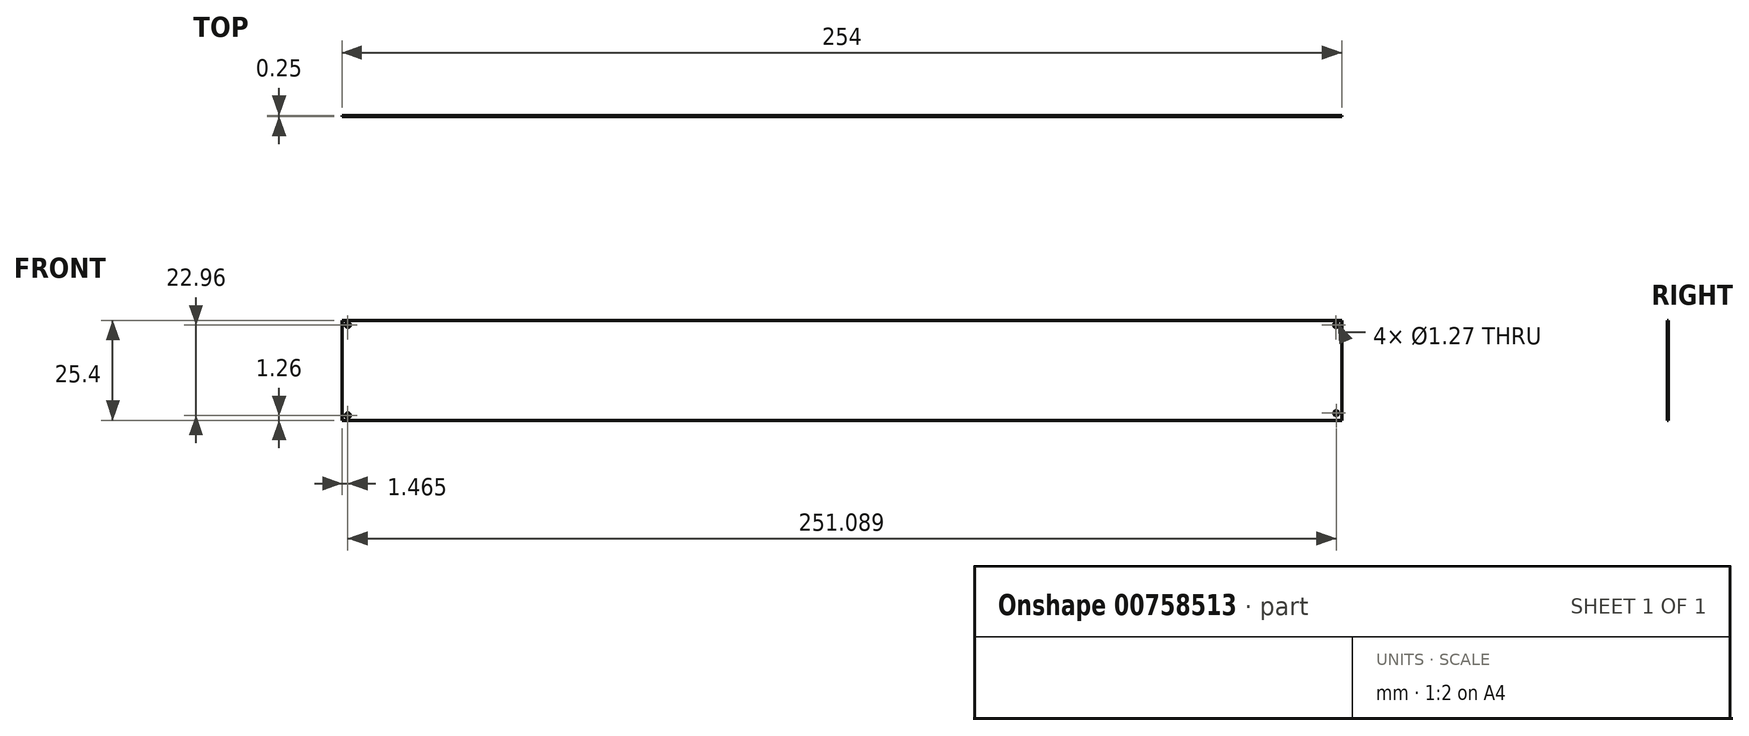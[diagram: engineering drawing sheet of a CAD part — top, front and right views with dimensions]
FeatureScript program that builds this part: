
annotation { "Feature Type Name" : "Feature", "Feature Type Description" : "" }
export const myFeature = defineFeature(function(context is Context, id is Id, definition is map)
    precondition{}
    {
        {
            var Q0;
            Q0=qCreatedBy(makeId("Front.planeOp"),FACE);
            var sketch = newSketch(context, id + "F0", { "sketchPlane" : qUnion([Q0])});
            skLineSegment(sketch, "E0.bottom", {"start": v(-49.32, 25.4) * mm, "end": v(204.68, 25.4) * mm});
            skLineSegment(sketch, "E0.top", {"start": v(-49.32, 0) * mm, "end": v(204.68, 0) * mm});
            skLineSegment(sketch, "E0.left", {"start": v(-49.32, 25.4) * mm, "end": v(-49.32, 0) * mm});
            skLineSegment(sketch, "E0.right", {"start": v(204.68, 25.4) * mm, "end": v(204.68, 0) * mm});
            skSolve(sketch);
        }
        {
            var Q0;
            Q0=makeQuery(id+"F0.imprint","IMPRINT",FACE,{"disambiguationData":[TD([[makeQuery(id+"F0.imprint","IMPRINT",EDGE,{"derivedFrom":sQuery(id+"F0.wireOp",EDGE,"E0.bottom")}),-1.0]])]});
            extrude(context, id + "F1", {"entities" : qUnion([Q0]), "depth" : 0.25 * mm, "offsetDistance" : 25.4 * mm});
        }
        {
            var Q0;
            Q0=makeQuery(id+"F1.opExtrude","CAP_FACE",FACE,{"disambiguationData":[OSD([sQuery(id+"F0.wireOp",EDGE,"E0.bottom"),sQuery(id+"F0.wireOp",EDGE,"E0.top"),sQuery(id+"F0.wireOp",EDGE,"E0.left"),sQuery(id+"F0.wireOp",EDGE,"E0.right")])],"isStart":false});
            var sketch = newSketch(context, id + "F2", { "sketchPlane" : qUnion([Q0])});
            skCircle(sketch, "E1", {"center": v(-47.85, 24.22) * mm, "radius": 0.77 * mm});
            skSolve(sketch);
        }
        {
            var Q0;
            Q0=sQuery(id+"F2.wireOp",VERTEX,"E1.center");
            var Q1;
            Q1=makeQuery(id+"F1.opExtrude","SWEPT_BODY",BODY,{"disambiguationData":[OSD([sQuery(id+"F0.wireOp",EDGE,"E0.bottom"),sQuery(id+"F0.wireOp",EDGE,"E0.top"),sQuery(id+"F0.wireOp",EDGE,"E0.left"),sQuery(id+"F0.wireOp",EDGE,"E0.right")])]});
            hole(context, id + "F3", {"style" : HoleStyle.SIMPLE, "endStyle" : HoleEndStyle.THROUGH, "holeDiameter" : 1.27 * mm, "majorDiameter" : 6.35 * mm, "isTappedThrough" : true, "tappedDepth" : 12.7 * mm, "tapClearance" : 3, "locations" : qUnion([Q0]), "scope" : qUnion([Q1])});
        }
        {
            var Q0;
            Q0=makeQuery(id+"F1.opExtrude","CAP_FACE",FACE,{"disambiguationData":[OSD([sQuery(id+"F0.wireOp",EDGE,"E0.bottom"),sQuery(id+"F0.wireOp",EDGE,"E0.top"),sQuery(id+"F0.wireOp",EDGE,"E0.left"),sQuery(id+"F0.wireOp",EDGE,"E0.right")])],"isStart":false});
            var sketch = newSketch(context, id + "F4", { "sketchPlane" : qUnion([Q0])});
            skLineSegment(sketch, "E2", {"start": v(-47.85, 24.22) * mm, "end": v(204.68, 24.22) * mm});
            skLineSegment(sketch, "E3", {"start": v(-47.85, 24.22) * mm, "end": v(-49.32, 24.22) * mm});
            skLineSegment(sketch, "E4", {"start": v(204.68, 24.22) * mm, "end": v(203.2, 24.22) * mm});
            skSolve(sketch);
        }
        {
            var Q0;
            Q0=sQuery(id+"F4.wireOp",VERTEX,"E4.end");
            var Q1;
            Q1=makeQuery(id+"F1.opExtrude","SWEPT_BODY",BODY,{"disambiguationData":[OSD([sQuery(id+"F0.wireOp",EDGE,"E0.bottom"),sQuery(id+"F0.wireOp",EDGE,"E0.top"),sQuery(id+"F0.wireOp",EDGE,"E0.left"),sQuery(id+"F0.wireOp",EDGE,"E0.right")])]});
            hole(context, id + "F5", {"style" : HoleStyle.SIMPLE, "endStyle" : HoleEndStyle.THROUGH, "holeDiameter" : 1.27 * mm, "majorDiameter" : 6.35 * mm, "isTappedThrough" : true, "tappedDepth" : 12.7 * mm, "tapClearance" : 3, "locations" : qUnion([Q0]), "scope" : qUnion([Q1])});
        }
        {
            var Q0;
            Q0=makeQuery(id+"F1.opExtrude","CAP_FACE",FACE,{"disambiguationData":[OSD([sQuery(id+"F0.wireOp",EDGE,"E0.bottom"),sQuery(id+"F0.wireOp",EDGE,"E0.top"),sQuery(id+"F0.wireOp",EDGE,"E0.left"),sQuery(id+"F0.wireOp",EDGE,"E0.right")])],"isStart":false});
            var sketch = newSketch(context, id + "F6", { "sketchPlane" : qUnion([Q0])});
            skLineSegment(sketch, "E5", {"start": v(-47.85, 24.22) * mm, "end": v(-47.85, 0) * mm});
            skSolve(sketch);
        }
        {
            var Q0;
            Q0=makeQuery(id+"F6.imprint","IMPRINT",FACE,{"disambiguationData":[TD([[makeQuery(id+"F6.imprint","IMPRINT",EDGE,{"derivedFrom":makeQuery(id+"F1.opExtrude","CAP_EDGE",EDGE,{"disambiguationData":[OSD([sQuery(id+"F0.wireOp",EDGE,"E0.bottom")])],"isStart":false})}),-1.0]])]});
            var sketch = newSketch(context, id + "F7", { "sketchPlane" : qUnion([Q0])});
            skCircle(sketch, "E6", {"center": v(-47.86, 1.26) * mm, "radius": 0.67 * mm});
            skSolve(sketch);
        }
        {
            var Q0;
            Q0=sQuery(id+"F7.wireOp",VERTEX,"E6.center");
            var Q1;
            Q1=makeQuery(id+"F1.opExtrude","SWEPT_BODY",BODY,{"disambiguationData":[OSD([sQuery(id+"F0.wireOp",EDGE,"E0.bottom"),sQuery(id+"F0.wireOp",EDGE,"E0.top"),sQuery(id+"F0.wireOp",EDGE,"E0.left"),sQuery(id+"F0.wireOp",EDGE,"E0.right")])]});
            hole(context, id + "F8", {"style" : HoleStyle.SIMPLE, "endStyle" : HoleEndStyle.THROUGH, "holeDiameter" : 1.27 * mm, "majorDiameter" : 6.35 * mm, "isTappedThrough" : true, "tappedDepth" : 12.7 * mm, "tapClearance" : 3, "locations" : qUnion([Q0]), "scope" : qUnion([Q1])});
        }
        {
            var Q0;
            Q0=makeQuery(id+"F6.imprint","IMPRINT",FACE,{"disambiguationData":[TD([[makeQuery(id+"F6.imprint","IMPRINT",EDGE,{"derivedFrom":makeQuery(id+"F1.opExtrude","CAP_EDGE",EDGE,{"disambiguationData":[OSD([sQuery(id+"F0.wireOp",EDGE,"E0.bottom")])],"isStart":false})}),-1.0]])]});
            var sketch = newSketch(context, id + "F9", { "sketchPlane" : qUnion([Q0])});
            skCircle(sketch, "E7", {"center": v(203.23, 1.83) * mm, "radius": 0.66 * mm});
            skSolve(sketch);
        }
        {
            var Q0;
            Q0=sQuery(id+"F9.wireOp",VERTEX,"E7.center");
            var Q1;
            Q1=makeQuery(id+"F1.opExtrude","SWEPT_BODY",BODY,{"disambiguationData":[OSD([sQuery(id+"F0.wireOp",EDGE,"E0.bottom"),sQuery(id+"F0.wireOp",EDGE,"E0.top"),sQuery(id+"F0.wireOp",EDGE,"E0.left"),sQuery(id+"F0.wireOp",EDGE,"E0.right")])]});
            hole(context, id + "F10", {"style" : HoleStyle.SIMPLE, "endStyle" : HoleEndStyle.THROUGH, "holeDiameter" : 1.27 * mm, "majorDiameter" : 6.35 * mm, "isTappedThrough" : true, "tappedDepth" : 12.7 * mm, "tapClearance" : 3, "locations" : qUnion([Q0]), "scope" : qUnion([Q1])});
        }
    });
